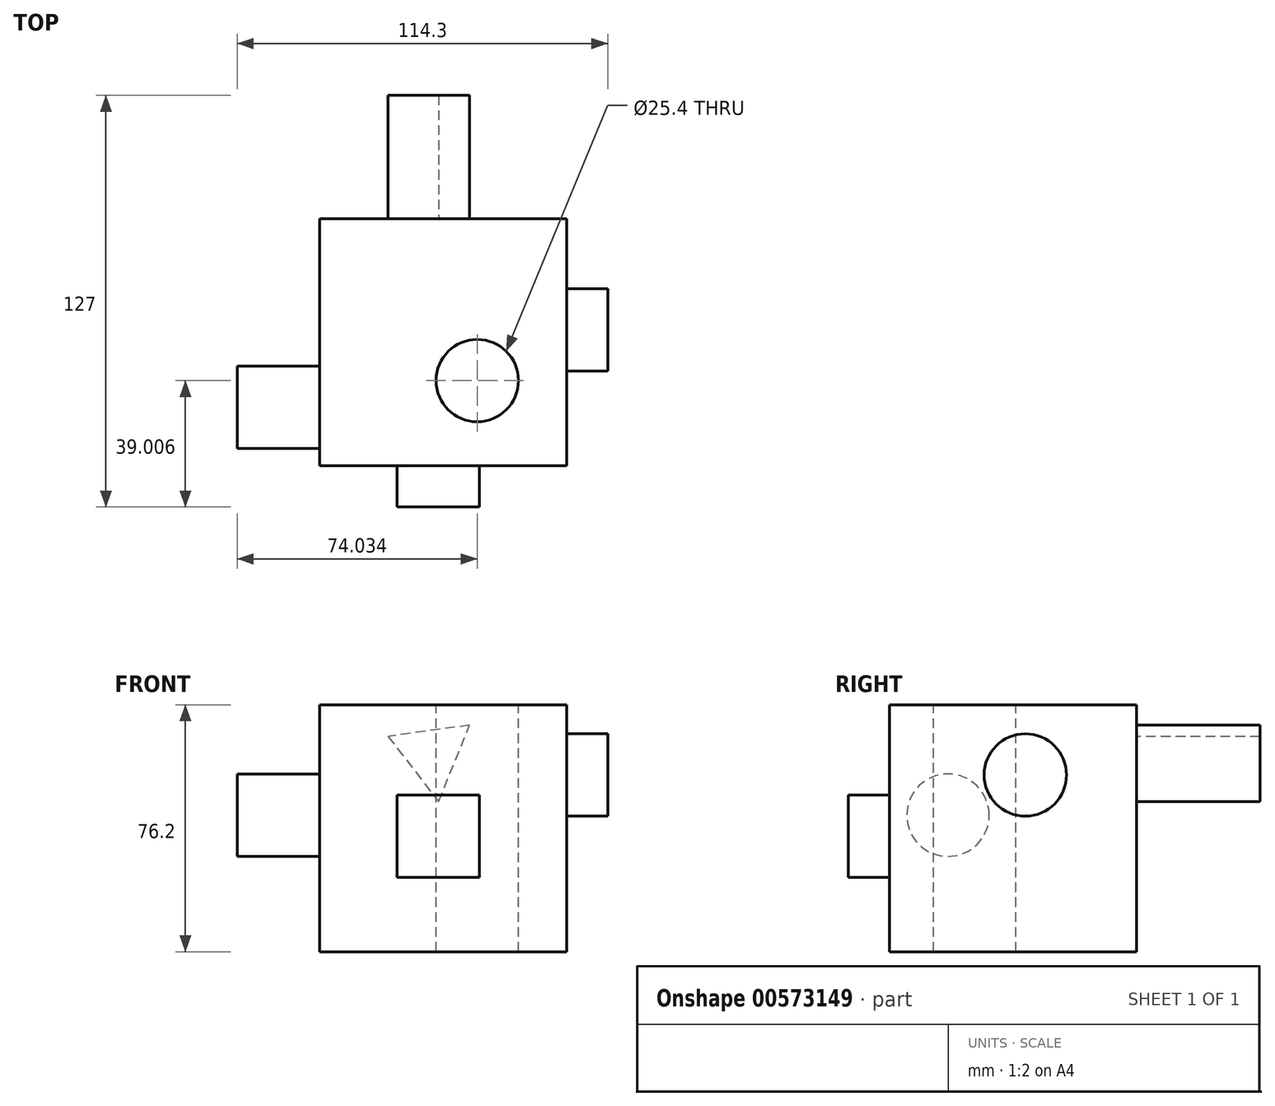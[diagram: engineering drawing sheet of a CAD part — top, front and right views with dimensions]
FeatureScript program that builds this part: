
annotation { "Feature Type Name" : "Feature", "Feature Type Description" : "" }
export const myFeature = defineFeature(function(context is Context, id is Id, definition is map)
    precondition{}
    {
        {
            var Q0;
            Q0=qCreatedBy(makeId("Front.planeOp"),FACE);
            var sketch = newSketch(context, id + "F0", { "sketchPlane" : qUnion([Q0])});
            skLineSegment(sketch, "E0.bottom", {"start": v(-59.55, 104.14) * mm, "end": v(16.65, 104.14) * mm});
            skLineSegment(sketch, "E0.top", {"start": v(-59.55, 27.94) * mm, "end": v(16.65, 27.94) * mm});
            skLineSegment(sketch, "E0.left", {"start": v(-59.55, 104.14) * mm, "end": v(-59.55, 27.94) * mm});
            skLineSegment(sketch, "E0.right", {"start": v(16.65, 104.14) * mm, "end": v(16.65, 27.94) * mm});
            skSolve(sketch);
        }
        {
            var Q0;
            Q0=makeQuery(id+"F0.imprint","IMPRINT",FACE,{"disambiguationData":[TD([[makeQuery(id+"F0.imprint","IMPRINT",EDGE,{"derivedFrom":sQuery(id+"F0.wireOp",EDGE,"E0.bottom")}),-1.0]])]});
            extrude(context, id + "F1", {"entities" : qUnion([Q0]), "depth" : 76.2 * mm, "offsetDistance" : 25.4 * mm});
        }
        {
            var Q0;
            Q0=makeQuery(id+"F1.opExtrude","CAP_FACE",FACE,{"disambiguationData":[OSD([sQuery(id+"F0.wireOp",EDGE,"E0.bottom"),sQuery(id+"F0.wireOp",EDGE,"E0.top"),sQuery(id+"F0.wireOp",EDGE,"E0.left"),sQuery(id+"F0.wireOp",EDGE,"E0.right")])],"isStart":false});
            var sketch = newSketch(context, id + "F2", { "sketchPlane" : qUnion([Q0])});
            skLineSegment(sketch, "E1.bottom", {"start": v(-35.67, 76.3) * mm, "end": v(-10.27, 76.3) * mm});
            skLineSegment(sketch, "E1.top", {"start": v(-35.67, 50.9) * mm, "end": v(-10.27, 50.9) * mm});
            skLineSegment(sketch, "E1.left", {"start": v(-35.67, 76.3) * mm, "end": v(-35.67, 50.9) * mm});
            skLineSegment(sketch, "E1.right", {"start": v(-10.27, 76.3) * mm, "end": v(-10.27, 50.9) * mm});
            skSolve(sketch);
        }
        {
            var Q0;
            Q0=makeQuery(id+"F2.imprint","IMPRINT",FACE,{"disambiguationData":[TD([[makeQuery(id+"F2.imprint","IMPRINT",EDGE,{"derivedFrom":sQuery(id+"F2.wireOp",EDGE,"E1.bottom")}),-1.0]])]});
            extrude(context, id + "F3", {"entities" : qUnion([Q0]), "operationType" : NewBodyOperationType.ADD, "depth" : 12.7 * mm, "offsetDistance" : 25.4 * mm});
        }
        {
            var Q0;
            Q0=makeQuery(id+"F1.opExtrude","SWEPT_FACE",FACE,{"disambiguationData":[OSD([sQuery(id+"F0.wireOp",EDGE,"E0.right")])]});
            var sketch = newSketch(context, id + "F4", { "sketchPlane" : qUnion([Q0])});
            skCircle(sketch, "E2", {"center": v(-34.3, 82.47) * mm, "radius": 12.7 * mm});
            skSolve(sketch);
        }
        {
            var Q0;
            Q0=makeQuery(id+"F4.imprint","IMPRINT",FACE,{"disambiguationData":[TD([[makeQuery(id+"F4.imprint","IMPRINT",EDGE,{"derivedFrom":sQuery(id+"F4.wireOp",EDGE,"E2")}),1.0]])]});
            extrude(context, id + "F5", {"entities" : qUnion([Q0]), "operationType" : NewBodyOperationType.ADD, "depth" : 12.7 * mm, "offsetDistance" : 25.4 * mm});
        }
        {
            var Q0;
            Q0=makeQuery(id+"F1.opExtrude","SWEPT_FACE",FACE,{"disambiguationData":[OSD([sQuery(id+"F0.wireOp",EDGE,"E0.bottom")])]});
            var sketch = newSketch(context, id + "F6", { "sketchPlane" : qUnion([Q0])});
            skPoint(sketch, "E3", {"position": v(-10.92, -49.9) * mm});
            skSolve(sketch);
        }
        {
            var Q0;
            Q0=sQuery(id+"F6.wireOp",VERTEX,"E3");
            var Q1;
            Q1=makeQuery(id+"F1.opExtrude","SWEPT_BODY",BODY,{"disambiguationData":[OSD([sQuery(id+"F0.wireOp",EDGE,"E0.bottom"),sQuery(id+"F0.wireOp",EDGE,"E0.top"),sQuery(id+"F0.wireOp",EDGE,"E0.left"),sQuery(id+"F0.wireOp",EDGE,"E0.right")])]});
            hole(context, id + "F7", {"style" : HoleStyle.SIMPLE, "endStyle" : HoleEndStyle.THROUGH, "holeDiameter" : 25.4 * mm, "isTappedThrough" : true, "tappedDepth" : 12.7 * mm, "tapClearance" : 3, "locations" : qUnion([Q0]), "scope" : qUnion([Q1])});
        }
        {
            var Q0;
            Q0=makeQuery(id+"F1.opExtrude","CAP_FACE",FACE,{"disambiguationData":[OSD([sQuery(id+"F0.wireOp",EDGE,"E0.bottom"),sQuery(id+"F0.wireOp",EDGE,"E0.top"),sQuery(id+"F0.wireOp",EDGE,"E0.left"),sQuery(id+"F0.wireOp",EDGE,"E0.right")])],"isStart":true});
            var sketch = newSketch(context, id + "F8", { "sketchPlane" : qUnion([Q0])});
            skLineSegment(sketch, "E4.0", {"start": v(22.83, 74.3) * mm, "end": v(13.24, 97.82) * mm});
            skLineSegment(sketch, "E4.1", {"start": v(13.24, 97.82) * mm, "end": v(38.4, 94.36) * mm});
            skLineSegment(sketch, "E4.2", {"start": v(38.4, 94.36) * mm, "end": v(22.83, 74.3) * mm});
            skPoint(sketch, "E4.0.midPoint", {"position": v(18.04, 86.06) * mm});
            skSolve(sketch);
        }
        {
            var Q0;
            Q0=makeQuery(id+"F8.imprint","IMPRINT",FACE,{"disambiguationData":[TD([[makeQuery(id+"F8.imprint","IMPRINT",EDGE,{"derivedFrom":sQuery(id+"F8.wireOp",EDGE,"E4.0")}),-1.0]])]});
            extrude(context, id + "F9", {"entities" : qUnion([Q0]), "operationType" : NewBodyOperationType.ADD, "depth" : 38.1 * mm, "offsetDistance" : 25.4 * mm});
        }
        {
            var Q0;
            Q0=makeQuery(id+"F1.opExtrude","SWEPT_FACE",FACE,{"disambiguationData":[OSD([sQuery(id+"F0.wireOp",EDGE,"E0.left")])]});
            var sketch = newSketch(context, id + "F10", { "sketchPlane" : qUnion([Q0])});
            skCircle(sketch, "E5", {"center": v(58.15, 70.06) * mm, "radius": 12.7 * mm});
            skPoint(sketch, "E6", {"position": v(59.63, 66.96) * mm});
            skSolve(sketch);
        }
        {
            var Q0;
            Q0=makeQuery(id+"F10.imprint","IMPRINT",FACE,{"disambiguationData":[TD([[makeQuery(id+"F10.imprint","IMPRINT",EDGE,{"derivedFrom":sQuery(id+"F10.wireOp",EDGE,"E5")}),1.0]])]});
            extrude(context, id + "F11", {"entities" : qUnion([Q0]), "operationType" : NewBodyOperationType.ADD, "depth" : 25.4 * mm, "offsetDistance" : 25.4 * mm});
        }
    });
